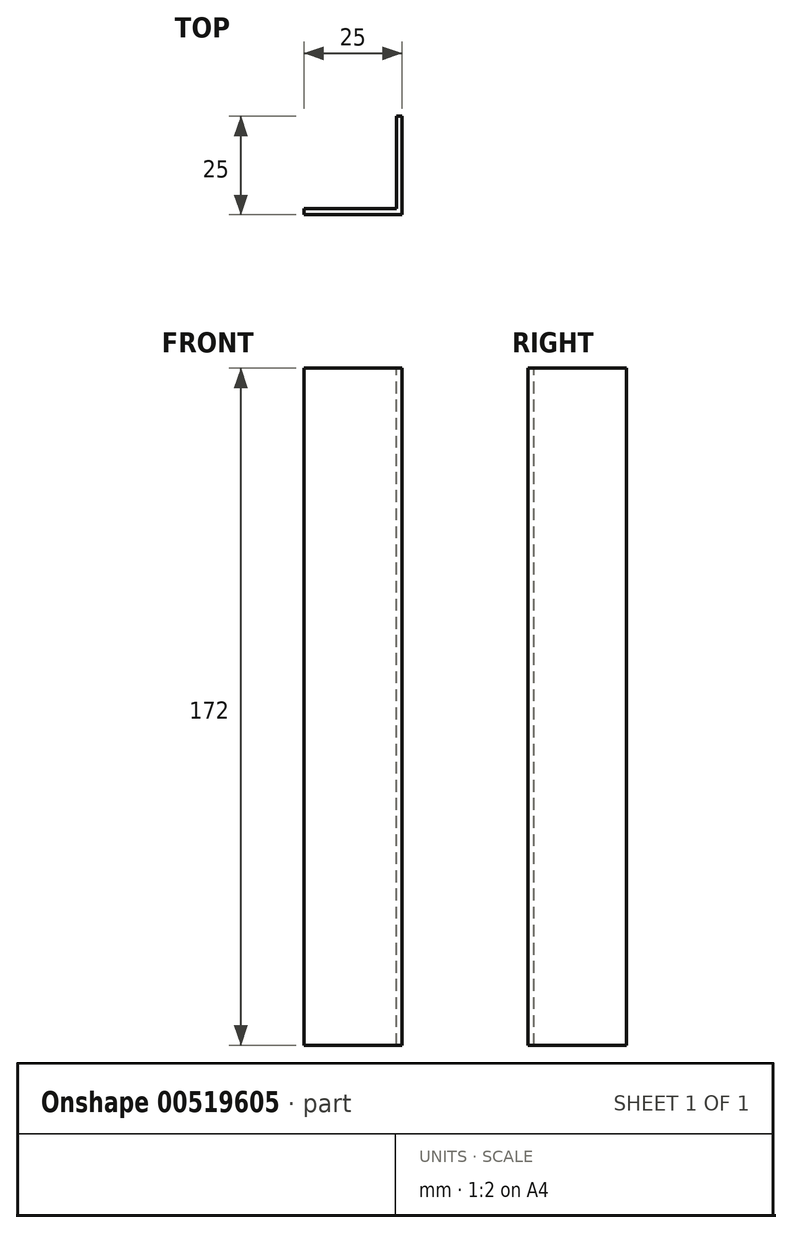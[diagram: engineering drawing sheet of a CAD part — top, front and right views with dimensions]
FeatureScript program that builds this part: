
annotation { "Feature Type Name" : "Feature", "Feature Type Description" : "" }
export const myFeature = defineFeature(function(context is Context, id is Id, definition is map)
    precondition{}
    {
        {
            var Q0;
            Q0=qCreatedBy(makeId("Top.planeOp"),FACE);
            var sketch = newSketch(context, id + "F0", { "sketchPlane" : qUnion([Q0])});
            skLineSegment(sketch, "E0.bottom", {"start": v(12.5, 0.75) * mm, "end": v(-12.5, 0.75) * mm});
            skLineSegment(sketch, "E0.top", {"start": v(12.5, -0.75) * mm, "end": v(-12.5, -0.75) * mm});
            skLineSegment(sketch, "E0.left", {"start": v(12.5, 0.75) * mm, "end": v(12.5, -0.75) * mm});
            skLineSegment(sketch, "E0.right", {"start": v(-12.5, 0.75) * mm, "end": v(-12.5, -0.75) * mm});
            skPoint(sketch, "E0.middle", {"position": v(0, 0) * mm});
            skLineSegment(sketch, "E1.bottom", {"start": v(12.5, -0.75) * mm, "end": v(11, -0.75) * mm});
            skLineSegment(sketch, "E1.top", {"start": v(12.5, 24.25) * mm, "end": v(11, 24.25) * mm});
            skLineSegment(sketch, "E1.left", {"start": v(12.5, -0.75) * mm, "end": v(12.5, 24.25) * mm});
            skLineSegment(sketch, "E1.right", {"start": v(11, -0.75) * mm, "end": v(11, 24.25) * mm});
            skSolve(sketch);
        }
        {
            var Q0;
            Q0 = qSketchRegion(id + "F0", true);
            extrude(context, id + "F1", {"entities" : qUnion([Q0]), "oppositeDirection" : true, "depth" : 172 * mm, "offsetDistance" : 25 * mm});
        }
    });
